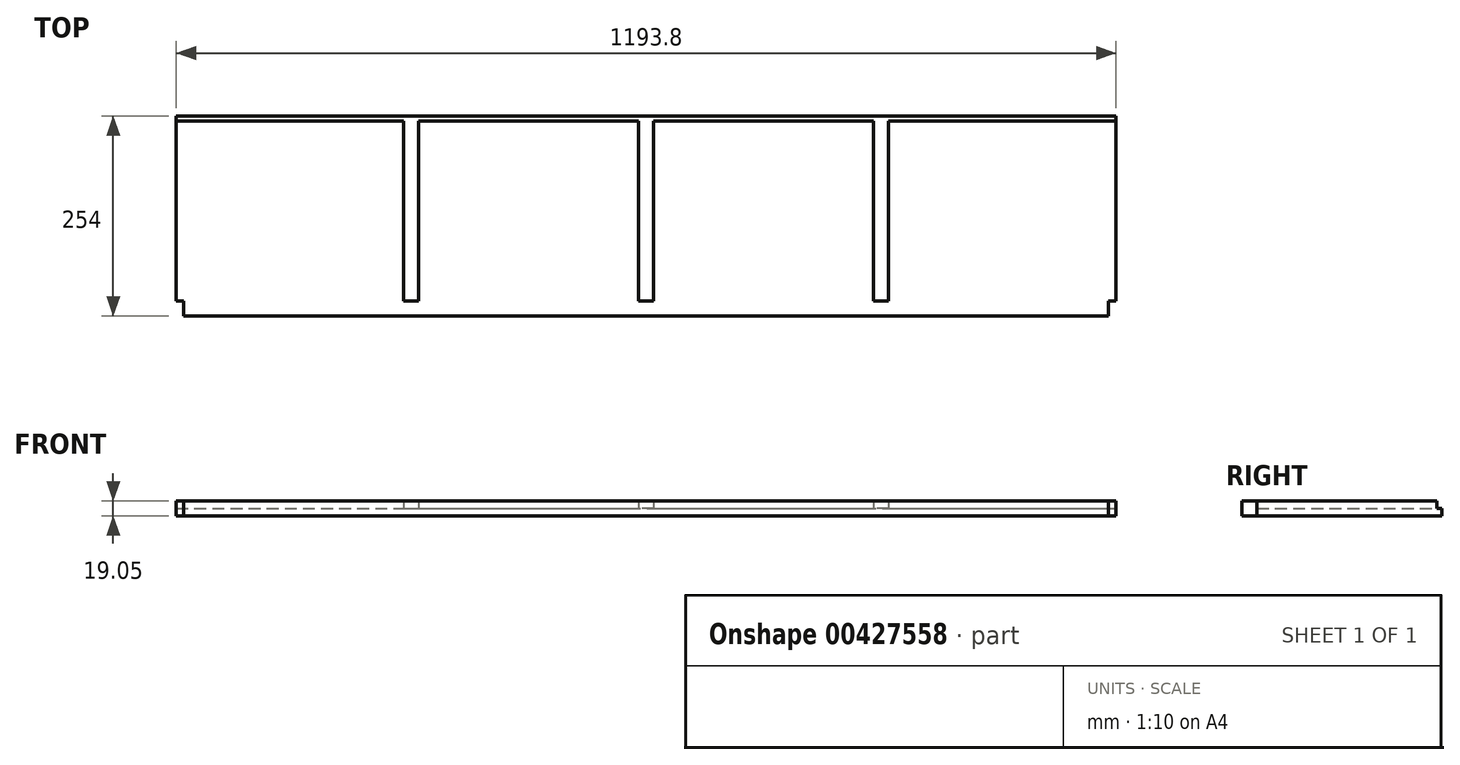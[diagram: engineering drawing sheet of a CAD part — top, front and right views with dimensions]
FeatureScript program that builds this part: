
annotation { "Feature Type Name" : "Feature", "Feature Type Description" : "" }
export const myFeature = defineFeature(function(context is Context, id is Id, definition is map)
    precondition{}
    {
        {
            var Q0;
            Q0=qCreatedBy(makeId("Top.planeOp"),FACE);
            var sketch = newSketch(context, id + "F0", { "sketchPlane" : qUnion([Q0])});
            skLineSegment(sketch, "E0.bottom", {"start": v(0, 0) * mm, "end": v(1193.8, 0) * mm});
            skLineSegment(sketch, "E0.top", {"start": v(0, 254) * mm, "end": v(1193.8, 254) * mm});
            skLineSegment(sketch, "E0.left", {"start": v(0, 0) * mm, "end": v(0, 254) * mm});
            skLineSegment(sketch, "E0.right", {"start": v(1193.8, 0) * mm, "end": v(1193.8, 254) * mm});
            skSolve(sketch);
        }
        {
            var Q0;
            Q0=qSketchRegion(id+"F0",true);
            extrude(context, id + "F1", {"entities" : qUnion([Q0]), "depth" : 19.05 * mm});
        }
        {
            var Q0;
            Q0=makeQuery(id+"F1.opExtrude","SWEPT_FACE",FACE,{"disambiguationData":[OSD([sQuery(id+"F0.wireOp",EDGE,"E0.top")])]});
            var sketch = newSketch(context, id + "F2", { "sketchPlane" : qUnion([Q0])});
            skLineSegment(sketch, "E1.bottom", {"start": v(-288.93, 19.05) * mm, "end": v(-307.98, 19.05) * mm});
            skLineSegment(sketch, "E1.top", {"start": v(-288.93, 9.52) * mm, "end": v(-307.98, 9.52) * mm});
            skLineSegment(sketch, "E1.left", {"start": v(-288.93, 19.05) * mm, "end": v(-288.93, 9.52) * mm});
            skLineSegment(sketch, "E1.right", {"start": v(-307.98, 19.05) * mm, "end": v(-307.98, 9.52) * mm});
            skLineSegment(sketch, "E2.bottom", {"start": v(-606.42, 19.05) * mm, "end": v(-587.38, 19.05) * mm});
            skLineSegment(sketch, "E2.top", {"start": v(-606.42, 9.52) * mm, "end": v(-587.38, 9.52) * mm});
            skLineSegment(sketch, "E2.left", {"start": v(-606.42, 19.05) * mm, "end": v(-606.42, 9.52) * mm});
            skLineSegment(sketch, "E2.right", {"start": v(-587.38, 19.05) * mm, "end": v(-587.38, 9.52) * mm});
            skLineSegment(sketch, "E3.bottom", {"start": v(-904.88, 19.05) * mm, "end": v(-885.83, 19.05) * mm});
            skLineSegment(sketch, "E3.top", {"start": v(-904.88, 9.52) * mm, "end": v(-885.83, 9.52) * mm});
            skLineSegment(sketch, "E3.left", {"start": v(-904.88, 19.05) * mm, "end": v(-904.88, 9.52) * mm});
            skLineSegment(sketch, "E3.right", {"start": v(-885.83, 19.05) * mm, "end": v(-885.83, 9.52) * mm});
            skSolve(sketch);
        }
        {
            var Q0;
            Q0=qSketchRegion(id+"F2",true);
            extrude(context, id + "F3", {"entities" : qUnion([Q0]), "operationType" : NewBodyOperationType.REMOVE, "oppositeDirection" : true, "depth" : 234.95 * mm});
        }
        {
            var Q0;
            Q0=makeQuery(id+"F1.opExtrude","CAP_FACE",FACE,{"disambiguationData":[OSD([sQuery(id+"F0.wireOp",EDGE,"E0.bottom"),sQuery(id+"F0.wireOp",EDGE,"E0.top"),sQuery(id+"F0.wireOp",EDGE,"E0.left"),sQuery(id+"F0.wireOp",EDGE,"E0.right")])],"isStart":false});
            var sketch = newSketch(context, id + "F4", { "sketchPlane" : qUnion([Q0])});
            skLineSegment(sketch, "E4.bottom", {"start": v(0, 254) * mm, "end": v(1193.8, 254) * mm});
            skLineSegment(sketch, "E4.top", {"start": v(0, 247.65) * mm, "end": v(1193.8, 247.65) * mm});
            skLineSegment(sketch, "E4.left", {"start": v(0, 254) * mm, "end": v(0, 247.65) * mm});
            skLineSegment(sketch, "E4.right", {"start": v(1193.8, 254) * mm, "end": v(1193.8, 247.65) * mm});
            skSolve(sketch);
        }
        {
            var Q0;
            Q0 = qSketchRegion(id + "F4", true);
            extrude(context, id + "F5", {"entities" : qUnion([Q0]), "operationType" : NewBodyOperationType.REMOVE, "oppositeDirection" : true, "depth" : 9.52 * mm});
        }
        {
            var Q0;
            Q0=makeQuery(id+"F1.opExtrude","CAP_FACE",FACE,{"disambiguationData":[OSD([sQuery(id+"F0.wireOp",EDGE,"E0.bottom"),sQuery(id+"F0.wireOp",EDGE,"E0.top"),sQuery(id+"F0.wireOp",EDGE,"E0.left"),sQuery(id+"F0.wireOp",EDGE,"E0.right")])],"isStart":false});
            var sketch = newSketch(context, id + "F6", { "sketchPlane" : qUnion([Q0])});
            skLineSegment(sketch, "E5.bottom", {"start": v(0, 0) * mm, "end": v(9.52, 0) * mm});
            skLineSegment(sketch, "E5.top", {"start": v(0, 19.05) * mm, "end": v(9.52, 19.05) * mm});
            skLineSegment(sketch, "E5.left", {"start": v(0, 0) * mm, "end": v(0, 19.05) * mm});
            skLineSegment(sketch, "E5.right", {"start": v(9.52, 0) * mm, "end": v(9.52, 19.05) * mm});
            skLineSegment(sketch, "E6.bottom", {"start": v(1193.8, 19.05) * mm, "end": v(1184.28, 19.05) * mm});
            skLineSegment(sketch, "E6.top", {"start": v(1193.8, 0) * mm, "end": v(1184.28, 0) * mm});
            skLineSegment(sketch, "E6.left", {"start": v(1193.8, 19.05) * mm, "end": v(1193.8, 0) * mm});
            skLineSegment(sketch, "E6.right", {"start": v(1184.28, 19.05) * mm, "end": v(1184.28, 0) * mm});
            skSolve(sketch);
        }
        {
            var Q0;
            Q0 = qSketchRegion(id + "F6", true);
            extrude(context, id + "F7", {"entities" : qUnion([Q0]), "operationType" : NewBodyOperationType.REMOVE, "oppositeDirection" : true, "depth" : 25.4 * mm});
        }
    });
